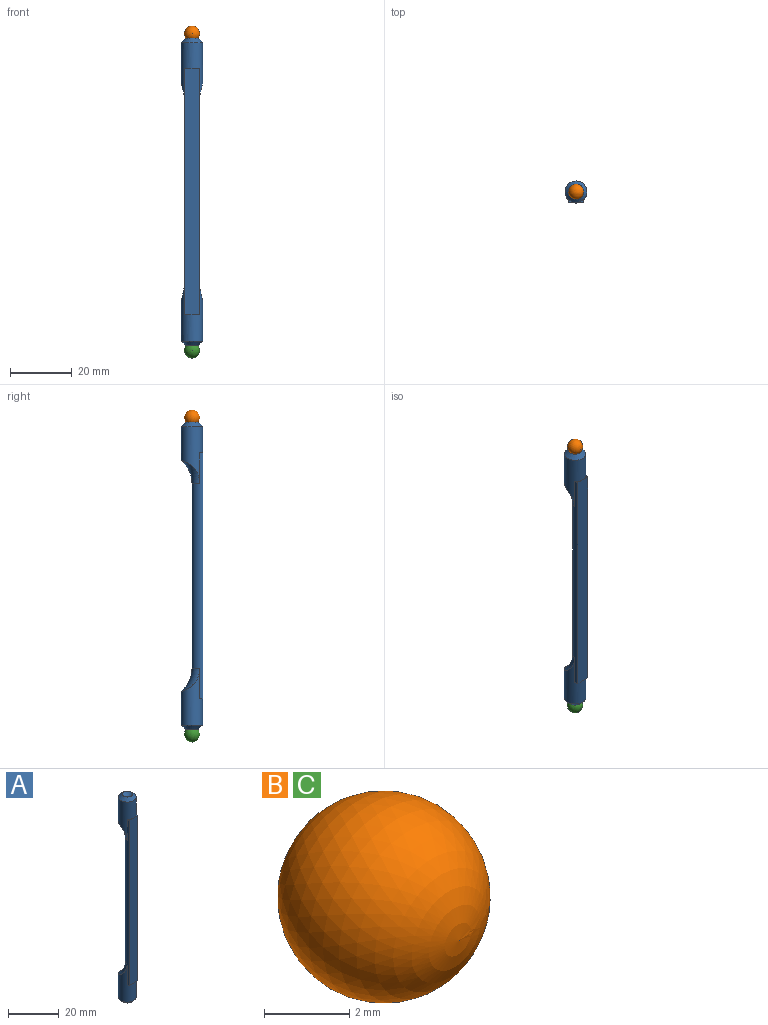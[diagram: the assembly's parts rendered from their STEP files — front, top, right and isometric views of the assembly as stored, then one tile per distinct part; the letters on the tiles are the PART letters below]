
ASSEMBLY  parts=3 mates=2
PART A: 14 faces, bbox 27.1x14.5x99.9 mm
  f0: plane 2.5x1.05mm, normal (0,0,1), area 0.7mm2, adj f1,f3,f4
  f1: cylinder r=2.5mm len=80mm, axis (0,0,-1), area 637.8mm2, adj f0,f2,f3,f4,f6,f8,f9,f10
  f2: plane 2.5x1.05mm, normal (0,0,1), area 0.7mm2, adj f1,f3,f4
  f3: plane 80x4.58mm, normal (0,-1,0), area 366.6mm2, adj f0,f1,f2,f8,f9
  f4: cylinder r=3.5mm len=18.5mm, axis (0,0,-1), area 252.4mm2, adj f0,f1,f2,f6,f7
  f5: sphere r=2.6mm, area 16.8mm2, adj f7
  f6: torus R=12.5mm, axis (0,0,1), area 65.4mm2, adj f1,f4
  f7: cone r=2mm half-angle=45deg, axis (0,0,-1), area 35.4mm2, adj f4,f5
  f8: plane 2.5x1.05mm, normal (0,0,-1), area 0.7mm2, adj f1,f3,f10
  f9: plane 2.5x1.05mm, normal (0,0,-1), area 0.7mm2, adj f1,f3,f10
  f10: cylinder r=3.5mm len=18.5mm, axis (0,0,1), area 252.4mm2, adj f1,f8,f9,f12,f13
  f11: sphere r=2.6mm, area 16.8mm2, adj f13
  f12: torus R=12.5mm, axis (0,0,-1), area 65.5mm2, adj f1,f10
  f13: cone r=2mm half-angle=45deg, axis (0,0,1), area 35.4mm2, adj f10,f11
PART B: 1 faces, bbox 5x5x5 mm
  f0: sphere r=2.5mm, area 78.5mm2
PART C: same geometry as B
PLACE A t=(1.29,-4.71,-49.12)mm
PLACE B t=(1.29,-1.21,37.3)mm
PLACE C t=(1.29,-1.21,-65.62)mm
MATE fastened C.f0 <-> A.f4  axis (0,0,1) through (1.29,-1.21,-65.62)mm
MATE fastened B.f0 <-> A.f4  axis (0,0,1) through (1.29,-1.21,37.3)mm
